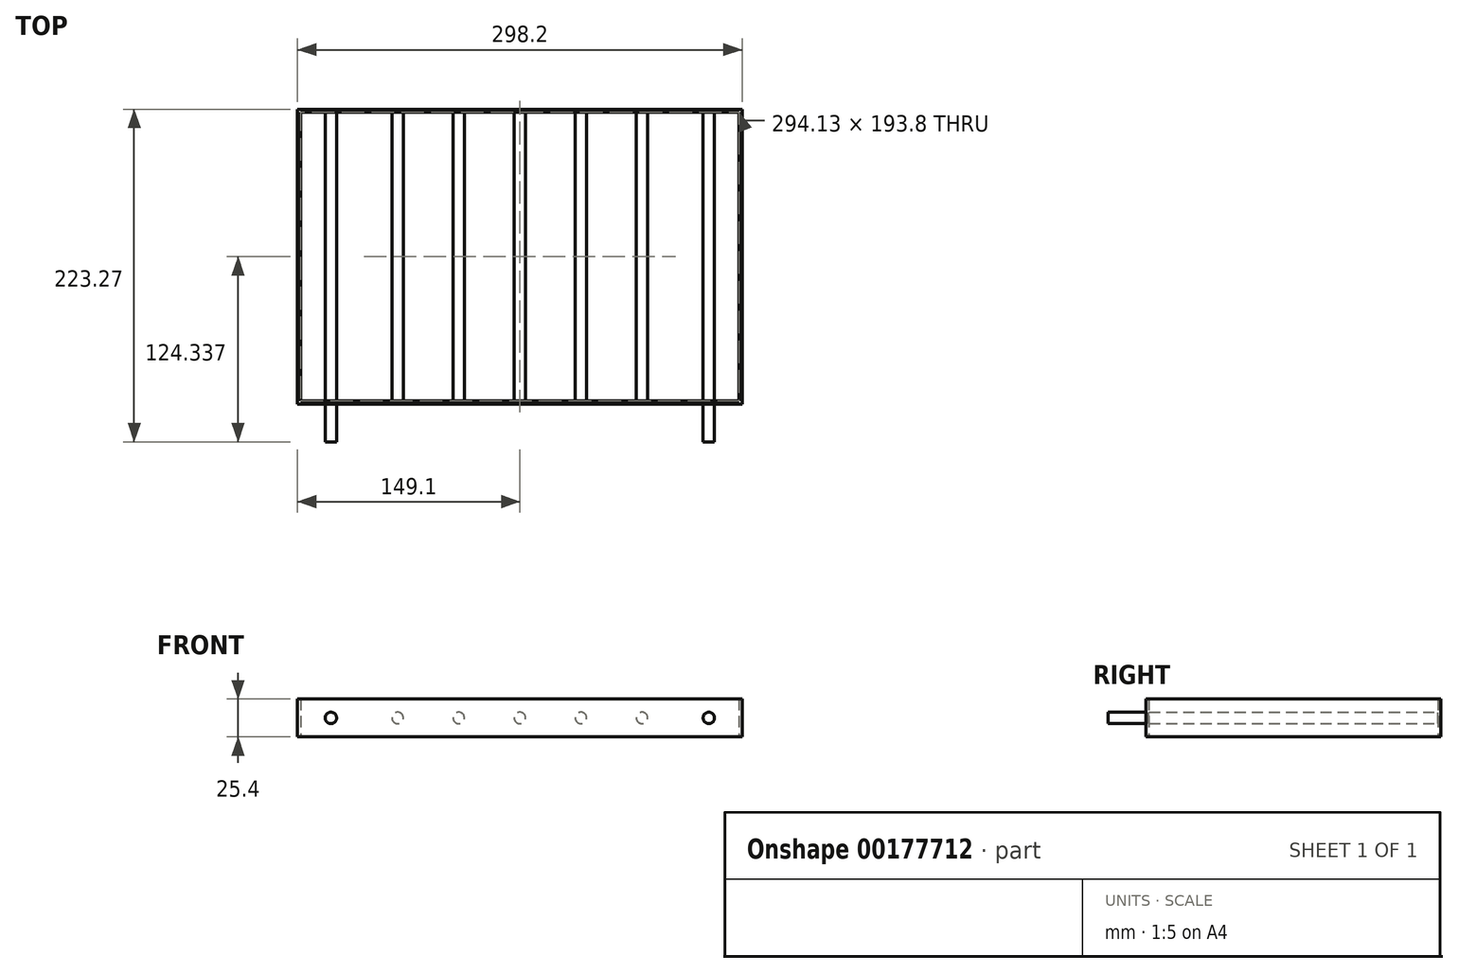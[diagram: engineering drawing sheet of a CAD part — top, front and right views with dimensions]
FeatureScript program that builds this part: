
annotation { "Feature Type Name" : "Feature", "Feature Type Description" : "" }
export const myFeature = defineFeature(function(context is Context, id is Id, definition is map)
    precondition{}
    {
        {
            var Q0;
            Q0=qCreatedBy(makeId("Front.planeOp"),FACE);
            var sketch = newSketch(context, id + "F0", { "sketchPlane" : qUnion([Q0])});
            skLineSegment(sketch, "E0.bottom", {"start": v(-149.1, 88.74) * mm, "end": v(149.1, 88.74) * mm});
            skLineSegment(sketch, "E0.top", {"start": v(-149.1, 63.34) * mm, "end": v(149.1, 63.34) * mm});
            skLineSegment(sketch, "E0.left", {"start": v(-149.1, 88.74) * mm, "end": v(-149.1, 63.34) * mm});
            skLineSegment(sketch, "E0.right", {"start": v(149.1, 88.74) * mm, "end": v(149.1, 63.34) * mm});
            skCircle(sketch, "E1", {"center": v(126.75, 76.04) * mm, "radius": 3.81 * mm, "construction": true});
            skCircle(sketch, "E2", {"center": v(-126.75, 76.04) * mm, "radius": 3.81 * mm, "construction": true});
            skSolve(sketch);
        }
        {
            var Q0;
            Q0=qSketchRegion(id+"F0",true);
            var Q1;
            Q1=sQuery(id+"F0.wireOp",EDGE,"E2");
            var Q2;
            Q2=sQuery(id+"F0.wireOp",EDGE,"E1");
            extrude(context, id + "F1", {"entities" : qUnion([Q0]), "surfaceEntities" : qUnion([Q1, Q2]), "depth" : 197.87 * mm});
        }
        {
            var Q0;
            Q0=makeQuery(id+"F1.opExtrude","SWEPT_FACE",FACE,{"disambiguationData":[OSD([sQuery(id+"F0.wireOp",EDGE,"E0.bottom")])]});
            shell(context, id + "F2", {"entities" : qUnion([Q0]), "thickness" : 2.03 * mm});
        }
        {
            var Q0;
            Q0=makeQuery(id+"F2.opShell","OFFSET_FACE",FACE,{"disambiguationData":[OSD([sQuery(id+"F0.wireOp",EDGE,"E0.top")])]});
            extrude(context, id + "F3", {"entities" : qUnion([Q0]), "operationType" : NewBodyOperationType.REMOVE, "oppositeDirection" : true, "depth" : 25.4 * mm});
        }
        {
            var Q0;
            Q0=makeQuery(id+"F1.opExtrude","CAP_FACE",FACE,{"disambiguationData":[OSD([sQuery(id+"F0.wireOp",EDGE,"E0.bottom"),sQuery(id+"F0.wireOp",EDGE,"E0.top"),sQuery(id+"F0.wireOp",EDGE,"E0.left"),sQuery(id+"F0.wireOp",EDGE,"E0.right")])],"isStart":false});
            var sketch = newSketch(context, id + "F4", { "sketchPlane" : qUnion([Q0])});
            skCircle(sketch, "E3.0", {"center": v(-126.75, 76.04) * mm, "radius": 3.81 * mm});
            skCircle(sketch, "E4.0", {"center": v(126.75, 76.04) * mm, "radius": 3.81 * mm});
            skSolve(sketch);
        }
        {
            var Q0;
            Q0=qSketchRegion(id+"F4",true);
            var Q1;
            {var subQ0=sQuery(id+"F0.wireOp",EDGE,"E0.top");var subQ1=sQuery(id+"F0.wireOp",EDGE,"E0.right");var subQ2=sQuery(id+"F0.wireOp",EDGE,"E0.left");var subQ3=sQuery(id+"F0.wireOp",EDGE,"E0.bottom");Q1=makeQuery(id+"F3.boolean.opBoolean","MERGE",FACE,{"derivedFrom":[makeQuery(id+"F2.opShell","OFFSET_FACE",FACE,{"disambiguationData":[OSD([subQ3,subQ0,subQ2,subQ1]),TDD([makeQuery(id+"F1.opExtrude","CAP_FACE",FACE,{"disambiguationData":[OSD([subQ3,subQ0,subQ2,subQ1])],"isStart":true})])]}),makeQuery(id+"F3.opExtrude","SWEPT_FACE",FACE,{"disambiguationData":[OSD([subQ0]),TDD([makeQuery(id+"F2.opShell","OFFSET_EDGE",EDGE,{"disambiguationData":[OSD([subQ0]),TDD([makeQuery(id+"F1.opExtrude","CAP_EDGE",EDGE,{"disambiguationData":[OSD([subQ0])],"isStart":true})])]})])]})]});}
            extrude(context, id + "F5", {"entities" : qUnion([Q0]), "operationType" : NewBodyOperationType.ADD, "depth" : 25.4 * mm, "hasSecondDirection" : true, "secondDirectionBound" : SecondDirectionBoundingType.UP_TO_SURFACE, "secondDirectionOppositeDirection" : true, "secondDirectionBoundEntityFace" : qUnion([Q1]), "secondDirectionDepth" : 25.4 * mm});
        }
        {
            var Q0;
            {var subQ0=sQuery(id+"F0.wireOp",EDGE,"E0.top");var subQ1=sQuery(id+"F0.wireOp",EDGE,"E0.right");var subQ2=sQuery(id+"F0.wireOp",EDGE,"E0.left");var subQ3=sQuery(id+"F0.wireOp",EDGE,"E0.bottom");Q0=makeQuery(id+"F3.boolean.opBoolean","MERGE",FACE,{"derivedFrom":[makeQuery(id+"F2.opShell","OFFSET_FACE",FACE,{"disambiguationData":[OSD([subQ3,subQ0,subQ2,subQ1]),TDD([makeQuery(id+"F1.opExtrude","CAP_FACE",FACE,{"disambiguationData":[OSD([subQ3,subQ0,subQ2,subQ1])],"isStart":true})])]}),makeQuery(id+"F3.opExtrude","SWEPT_FACE",FACE,{"disambiguationData":[OSD([subQ0]),TDD([makeQuery(id+"F2.opShell","OFFSET_EDGE",EDGE,{"disambiguationData":[OSD([subQ0]),TDD([makeQuery(id+"F1.opExtrude","CAP_EDGE",EDGE,{"disambiguationData":[OSD([subQ0])],"isStart":true})])]})])]})]});}
            var sketch = newSketch(context, id + "F6", { "sketchPlane" : qUnion([Q0])});
            skCircle(sketch, "E5.0", {"center": v(-126.75, 76.04) * mm, "radius": 3.81 * mm, "construction": true});
            skCircle(sketch, "E6.0", {"center": v(126.75, 76.04) * mm, "radius": 3.81 * mm});
            skCircle(sketch, "E7", {"center": v(-81.96, 76.04) * mm, "radius": 3.81 * mm});
            skCircle(sketch, "E8", {"center": v(-40.98, 76.04) * mm, "radius": 3.81 * mm});
            skCircle(sketch, "E9", {"center": v(0, 76.04) * mm, "radius": 3.81 * mm});
            skCircle(sketch, "E10", {"center": v(40.98, 76.04) * mm, "radius": 3.81 * mm});
            skCircle(sketch, "E11", {"center": v(81.95, 76.04) * mm, "radius": 3.81 * mm});
            skSolve(sketch);
        }
        {
            var Q0;
            Q0 = qSketchRegion(id + "F6", true);
            extrude(context, id + "F7", {"entities" : qUnion([Q0]), "operationType" : NewBodyOperationType.ADD, "endBound" : BoundingType.UP_TO_NEXT, "depth" : 25.4 * mm});
        }
    });
